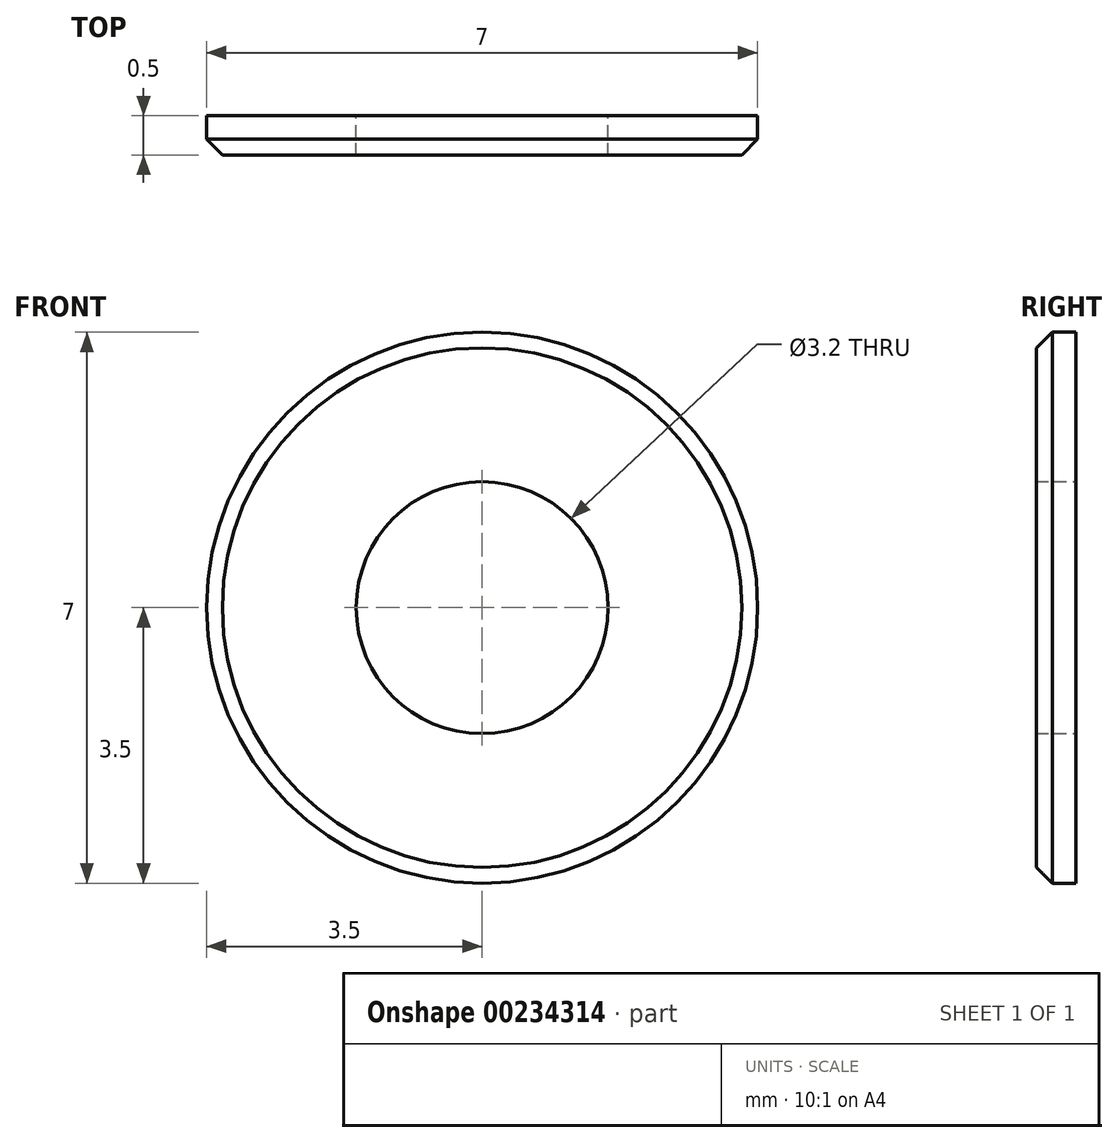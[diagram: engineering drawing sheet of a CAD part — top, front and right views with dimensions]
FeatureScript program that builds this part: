
annotation { "Feature Type Name" : "Feature", "Feature Type Description" : "" }
export const myFeature = defineFeature(function(context is Context, id is Id, definition is map)
    precondition{}
    {
        {
            var Q0;
            Q0=qCreatedBy(makeId("Front.planeOp"),FACE);
            var sketch = newSketch(context, id + "F0", { "sketchPlane" : qUnion([Q0])});
            skCircle(sketch, "E0", {"center": v(0, 0) * mm, "radius": 1.6 * mm});
            skCircle(sketch, "E1", {"center": v(0, 0) * mm, "radius": 3.5 * mm});
            skSolve(sketch);
        }
        {
            var Q0;
            Q0=makeQuery(id+"F0.imprint","IMPRINT",FACE,{"disambiguationData":[TD([[makeQuery(id+"F0.imprint","IMPRINT",EDGE,{"derivedFrom":sQuery(id+"F0.wireOp",EDGE,"E0")}),-1.0]])]});
            extrude(context, id + "F1", {"entities" : qUnion([Q0]), "depth" : .5 * mm});
        }
        {
            var Q0;
            Q0=makeQuery(id+"F1.opExtrude","CAP_EDGE",EDGE,{"disambiguationData":[OSD([sQuery(id+"F0.wireOp",EDGE,"E1")])],"isStart":false});
            chamfer(context, id + "F2", {"entities" : qUnion([Q0]), "width" : .2 * mm, "tangentPropagation" : true});
        }
    });
